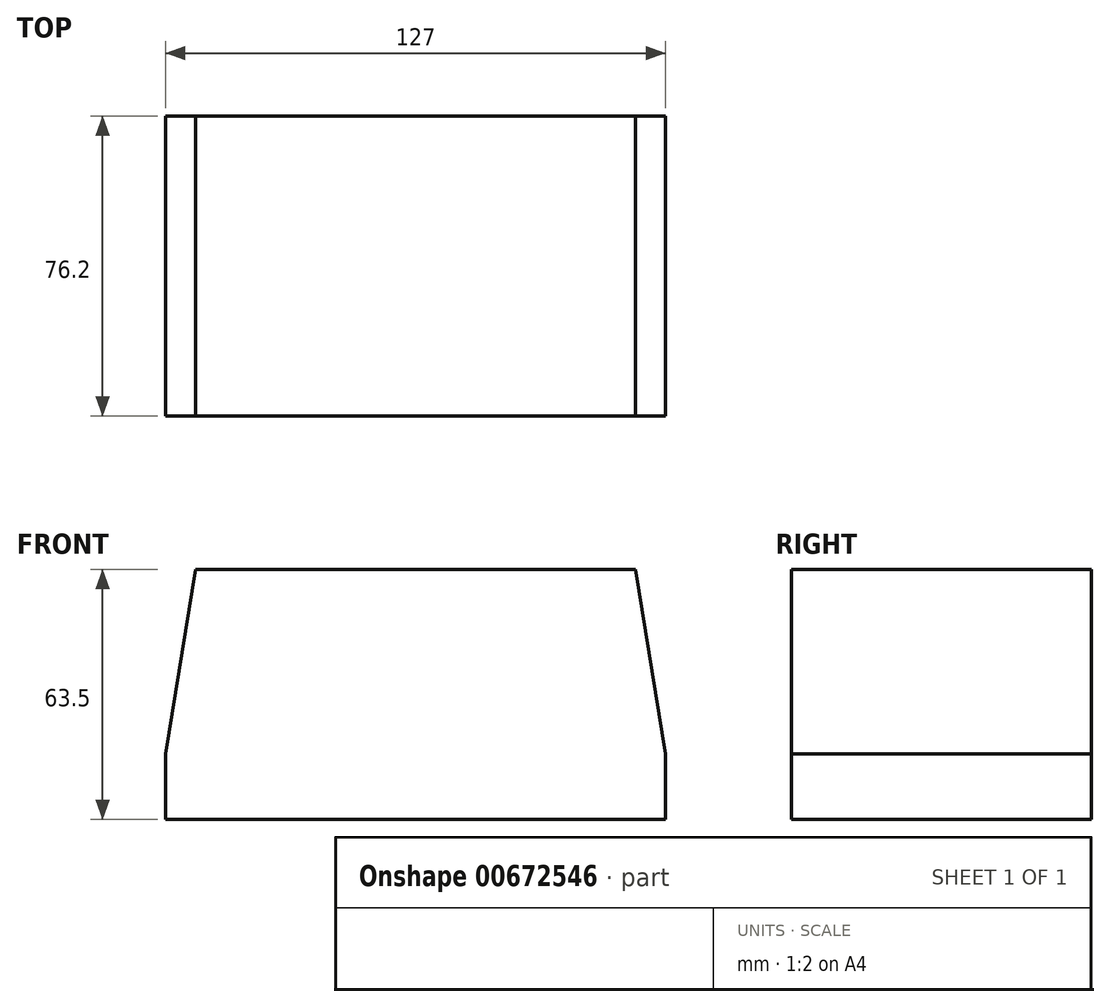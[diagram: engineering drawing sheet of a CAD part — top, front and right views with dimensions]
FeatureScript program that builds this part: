
annotation { "Feature Type Name" : "Feature", "Feature Type Description" : "" }
export const myFeature = defineFeature(function(context is Context, id is Id, definition is map)
    precondition{}
    {
        {
            var Q0;
            Q0=qCreatedBy(makeId("Top.planeOp"),FACE);
            var sketch = newSketch(context, id + "F0", { "sketchPlane" : qUnion([Q0])});
            skLineSegment(sketch, "E0.bottom", {"start": v(-64.18, 40.8) * mm, "end": v(62.82, 40.8) * mm});
            skLineSegment(sketch, "E0.top", {"start": v(-64.18, -35.4) * mm, "end": v(62.82, -35.4) * mm});
            skLineSegment(sketch, "E0.left", {"start": v(-64.18, 40.8) * mm, "end": v(-64.18, -35.4) * mm});
            skLineSegment(sketch, "E0.right", {"start": v(62.82, 40.8) * mm, "end": v(62.82, -35.4) * mm});
            skSolve(sketch);
        }
        {
            var Q0;
            Q0=makeQuery(id+"F0.imprint","IMPRINT",FACE,{"disambiguationData":[TD([[makeQuery(id+"F0.imprint","IMPRINT",EDGE,{"derivedFrom":sQuery(id+"F0.wireOp",EDGE,"E0.bottom")}),-1.0]])]});
            extrude(context, id + "F1", {"entities" : qUnion([Q0]), "depth" : 0.76 * mm, "offsetDistance" : 25.4 * mm});
        }
        {
            var Q0;
            Q0=makeQuery(id+"F1.opExtrude","SWEPT_FACE",FACE,{"disambiguationData":[OSD([sQuery(id+"F0.wireOp",EDGE,"E0.top")])]});
            var sketch = newSketch(context, id + "F2", { "sketchPlane" : qUnion([Q0])});
            skLineSegment(sketch, "E1", {"start": v(62.82, 0) * mm, "end": v(62.82, 16.66) * mm});
            skLineSegment(sketch, "E2", {"start": v(-64.18, 16.66) * mm, "end": v(-64.18, 0.76) * mm});
            skLineSegment(sketch, "E3.bottom", {"start": v(-56.56, 63.5) * mm, "end": v(55.2, 63.5) * mm});
            skLineSegment(sketch, "E4", {"start": v(-56.56, 63.5) * mm, "end": v(-64.18, 16.66) * mm});
            skLineSegment(sketch, "E5", {"start": v(62.82, 16.66) * mm, "end": v(55.2, 63.5) * mm});
            skSolve(sketch);
        }
        {
            var Q0;
            Q0=makeQuery(id+"F2.imprint","IMPRINT",FACE,{"disambiguationData":[TD([[makeQuery(id+"F2.imprint","IMPRINT",EDGE,{"derivedFrom":sQuery(id+"F2.wireOp",EDGE,"E2")}),1.0]])]});
            extrude(context, id + "F3", {"entities" : qUnion([Q0]), "operationType" : NewBodyOperationType.ADD, "oppositeDirection" : true, "depth" : 76.2 * mm, "offsetDistance" : 25.4 * mm});
        }
    });
